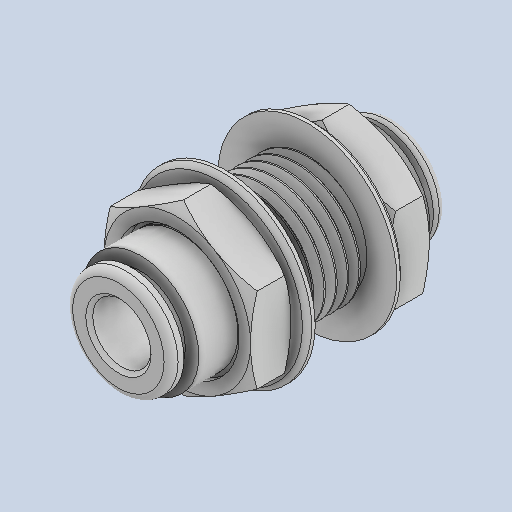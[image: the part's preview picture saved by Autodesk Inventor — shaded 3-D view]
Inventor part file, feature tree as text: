
AUTODESK INVENTOR PART (.ipt)
format: ipt  version: 2025 (Build 290162000, 162)  size: 635,392 bytes
history: native  units: mm
features: other x1, extrude x1
ambient origin geometry x8: Origin, YZ Plane, XZ Plane, XY Plane, X Axis, Y Axis, Z Axis, Center Point
bodies: Solid1 (feature_tree), Solid2 (feature_tree)
feature tree (2):
  other  "Cut-Extrude8"
  extrude  "Extrude5"  [1 undecoded]
note: 1 required parameter value undecoded (feature->parameter linkage not recoverable at this tier; creation-order binding heuristic only, values carry confidence <= 0.55)
